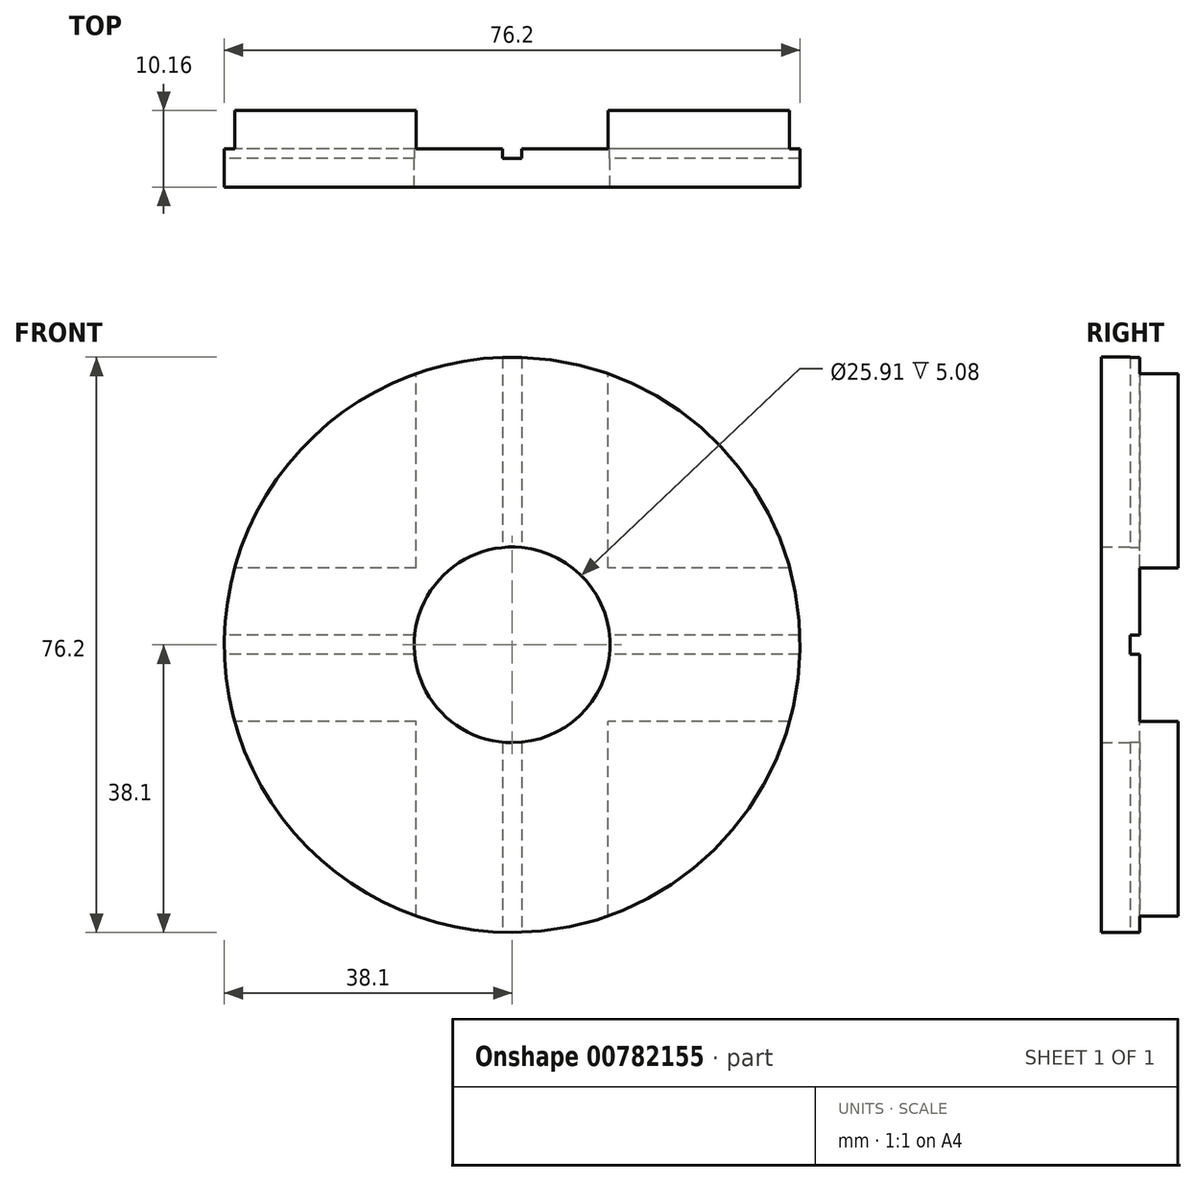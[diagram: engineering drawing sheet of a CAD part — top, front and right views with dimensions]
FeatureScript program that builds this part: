
annotation { "Feature Type Name" : "Feature", "Feature Type Description" : "" }
export const myFeature = defineFeature(function(context is Context, id is Id, definition is map)
    precondition{}
    {
        {
            var Q0;
            Q0=qCreatedBy(makeId("Front.planeOp"),FACE);
            var sketch = newSketch(context, id + "F0", { "sketchPlane" : qUnion([Q0])});
            skCircle(sketch, "E0", {"center": v(0, 0) * mm, "radius": 12.7 * mm});
            skSolve(sketch);
        }
        {
            var Q0;
            Q0=qSketchRegion(id+"F0",true);
            extrude(context, id + "F1", {"entities" : qUnion([Q0]), "depth" : 17.78 * mm, "offsetDistance" : 25.4 * mm});
        }
        {
            var Q0;
            Q0=qCreatedBy(makeId("Front.planeOp"),FACE);
            var sketch = newSketch(context, id + "F2", { "sketchPlane" : qUnion([Q0])});
            skCircle(sketch, "E1", {"center": v(0, 0) * mm, "radius": 38.1 * mm});
            skSolve(sketch);
        }
        {
            var Q0;
            Q0=qSketchRegion(id+"F2",true);
            extrude(context, id + "F3", {"entities" : qUnion([Q0]), "operationType" : NewBodyOperationType.ADD, "depth" : 10.16 * mm, "offsetDistance" : 25.4 * mm});
        }
        {
            var Q0;
            Q0=qCreatedBy(makeId("Front.planeOp"),FACE);
            var sketch = newSketch(context, id + "F4", { "sketchPlane" : qUnion([Q0])});
            skCircle(sketch, "E2", {"center": v(0, 0) * mm, "radius": 12.95 * mm});
            skSolve(sketch);
        }
        {
            var Q0;
            Q0=qSketchRegion(id+"F4",true);
            extrude(context, id + "F5", {"entities" : qUnion([Q0]), "operationType" : NewBodyOperationType.REMOVE, "endBound" : BoundingType.THROUGH_ALL, "depth" : 25.4 * mm, "offsetDistance" : 25.4 * mm, "hasSecondDirection" : true, "secondDirectionBound" : SecondDirectionBoundingType.THROUGH_ALL, "secondDirectionOppositeDirection" : true, "secondDirectionDepth" : 25.4 * mm});
        }
        {
            var Q0;
            Q0=qCreatedBy(makeId("Right.planeOp"),FACE);
            var sketch = newSketch(context, id + "F6", { "sketchPlane" : qUnion([Q0])});
            skLineSegment(sketch, "E3.bottom", {"start": v(0, 10.16) * mm, "end": v(-5.08, 10.16) * mm});
            skLineSegment(sketch, "E3.top", {"start": v(0, -10.16) * mm, "end": v(-5.08, -10.16) * mm});
            skLineSegment(sketch, "E3.left", {"start": v(0, 10.16) * mm, "end": v(0, -10.16) * mm});
            skLineSegment(sketch, "E3.right", {"start": v(-5.08, 10.16) * mm, "end": v(-5.08, -10.16) * mm});
            skSolve(sketch);
        }
        {
            var Q0;
            Q0=qSketchRegion(id+"F6",true);
            extrude(context, id + "F7", {"entities" : qUnion([Q0]), "operationType" : NewBodyOperationType.REMOVE, "endBound" : BoundingType.THROUGH_ALL, "depth" : 25.4 * mm, "offsetDistance" : 25.4 * mm, "hasSecondDirection" : true, "secondDirectionBound" : SecondDirectionBoundingType.THROUGH_ALL, "secondDirectionOppositeDirection" : true, "secondDirectionDepth" : 25.4 * mm});
        }
        {
            var Q0;
            Q0=qCreatedBy(makeId("Top.planeOp"),FACE);
            var sketch = newSketch(context, id + "F8", { "sketchPlane" : qUnion([Q0])});
            skLineSegment(sketch, "E4.bottom", {"start": v(-12.7, 0) * mm, "end": v(12.7, 0) * mm});
            skLineSegment(sketch, "E4.top", {"start": v(-12.7, -5.08) * mm, "end": v(12.7, -5.08) * mm});
            skLineSegment(sketch, "E4.left", {"start": v(-12.7, 0) * mm, "end": v(-12.7, -5.08) * mm});
            skLineSegment(sketch, "E4.right", {"start": v(12.7, 0) * mm, "end": v(12.7, -5.08) * mm});
            skSolve(sketch);
        }
        {
            var Q0;
            Q0=qSketchRegion(id+"F8",true);
            extrude(context, id + "F9", {"entities" : qUnion([Q0]), "operationType" : NewBodyOperationType.REMOVE, "endBound" : BoundingType.THROUGH_ALL, "oppositeDirection" : true, "depth" : 25.4 * mm, "offsetDistance" : 25.4 * mm, "hasSecondDirection" : true, "secondDirectionBound" : SecondDirectionBoundingType.THROUGH_ALL, "secondDirectionOppositeDirection" : false, "secondDirectionDepth" : 25.4 * mm});
        }
        {
            var Q0;
            {var subQ0=sQuery(id+"F2.wireOp",EDGE,"E1");var subQ2=makeQuery(id+"F7.opExtrude","SWEPT_FACE",FACE,{"disambiguationData":[OSD([sQuery(id+"F6.wireOp",EDGE,"E3.bottom")])]});Q0=makeQuery(id+"F9.boolean.opBoolean","SPLIT",FACE,{"disambiguationData":[TD([makeQuery(id+"F7.boolean.opBoolean","COPY",FACE,{"disambiguationData":[OD(1.0)],"derivedFrom":subQ2})])],"derivedFrom":makeQuery(id+"F7.boolean.opBoolean","SPLIT",FACE,{"disambiguationData":[TD([subQ2])],"derivedFrom":makeQuery(id+"F3.boolean.opBoolean","MERGE",FACE,{"derivedFrom":[makeQuery(id+"F1.opExtrude","CAP_FACE",FACE,{"disambiguationData":[OSD([sQuery(id+"F0.wireOp",EDGE,"E0")])],"isStart":true}),makeQuery(id+"F3.opExtrude","CAP_FACE",FACE,{"disambiguationData":[OSD([subQ0])],"isStart":true})]})})});}
            var sketch = newSketch(context, id + "F10", { "sketchPlane" : qUnion([Q0])});
            skArc(sketch, "E5.0", {"start": v(38.08, -1.27) * mm, "mid": v(38.1, 0) * mm, "end": v(38.08, 1.27) * mm});
            skLineSegment(sketch, "E6.left", {"start": v(-1.27, 38.08) * mm, "end": v(-1.27, 1.27) * mm});
            skLineSegment(sketch, "E6.right", {"start": v(1.27, 38.08) * mm, "end": v(1.27, 1.27) * mm});
            skLineSegment(sketch, "E7.bottom", {"start": v(-38.08, 1.27) * mm, "end": v(-1.27, 1.27) * mm});
            skLineSegment(sketch, "E7.top", {"start": v(-38.08, -1.27) * mm, "end": v(-1.27, -1.27) * mm});
            skLineSegment(sketch, "E8.trimOffspring", {"start": v(1.27, 1.27) * mm, "end": v(38.08, 1.27) * mm});
            skLineSegment(sketch, "E9.trimOffspring", {"start": v(-1.27, -1.27) * mm, "end": v(-1.27, -38.08) * mm});
            skLineSegment(sketch, "E10.trimOffspring", {"start": v(1.27, -1.27) * mm, "end": v(38.08, -1.27) * mm});
            skLineSegment(sketch, "E11.trimOffspring", {"start": v(1.27, -1.27) * mm, "end": v(1.27, -38.08) * mm});
            skArc(sketch, "E12.trimOffspring", {"start": v(-1.27, -38.08) * mm, "mid": v(0, -38.1) * mm, "end": v(1.27, -38.08) * mm});
            skArc(sketch, "E13.trimOffspring", {"start": v(-38.08, 1.27) * mm, "mid": v(-38.1, 0) * mm, "end": v(-38.08, -1.27) * mm});
            skArc(sketch, "E14.trimOffspring", {"start": v(1.27, 38.08) * mm, "mid": v(0, 38.1) * mm, "end": v(-1.27, 38.08) * mm});
            skSolve(sketch);
        }
        {
            var Q0;
            Q0 = qSketchRegion(id + "F10", true);
            extrude(context, id + "F11", {"entities" : qUnion([Q0]), "operationType" : NewBodyOperationType.REMOVE, "oppositeDirection" : true, "depth" : 6.35 * mm, "offsetDistance" : 25.4 * mm});
        }
    });
